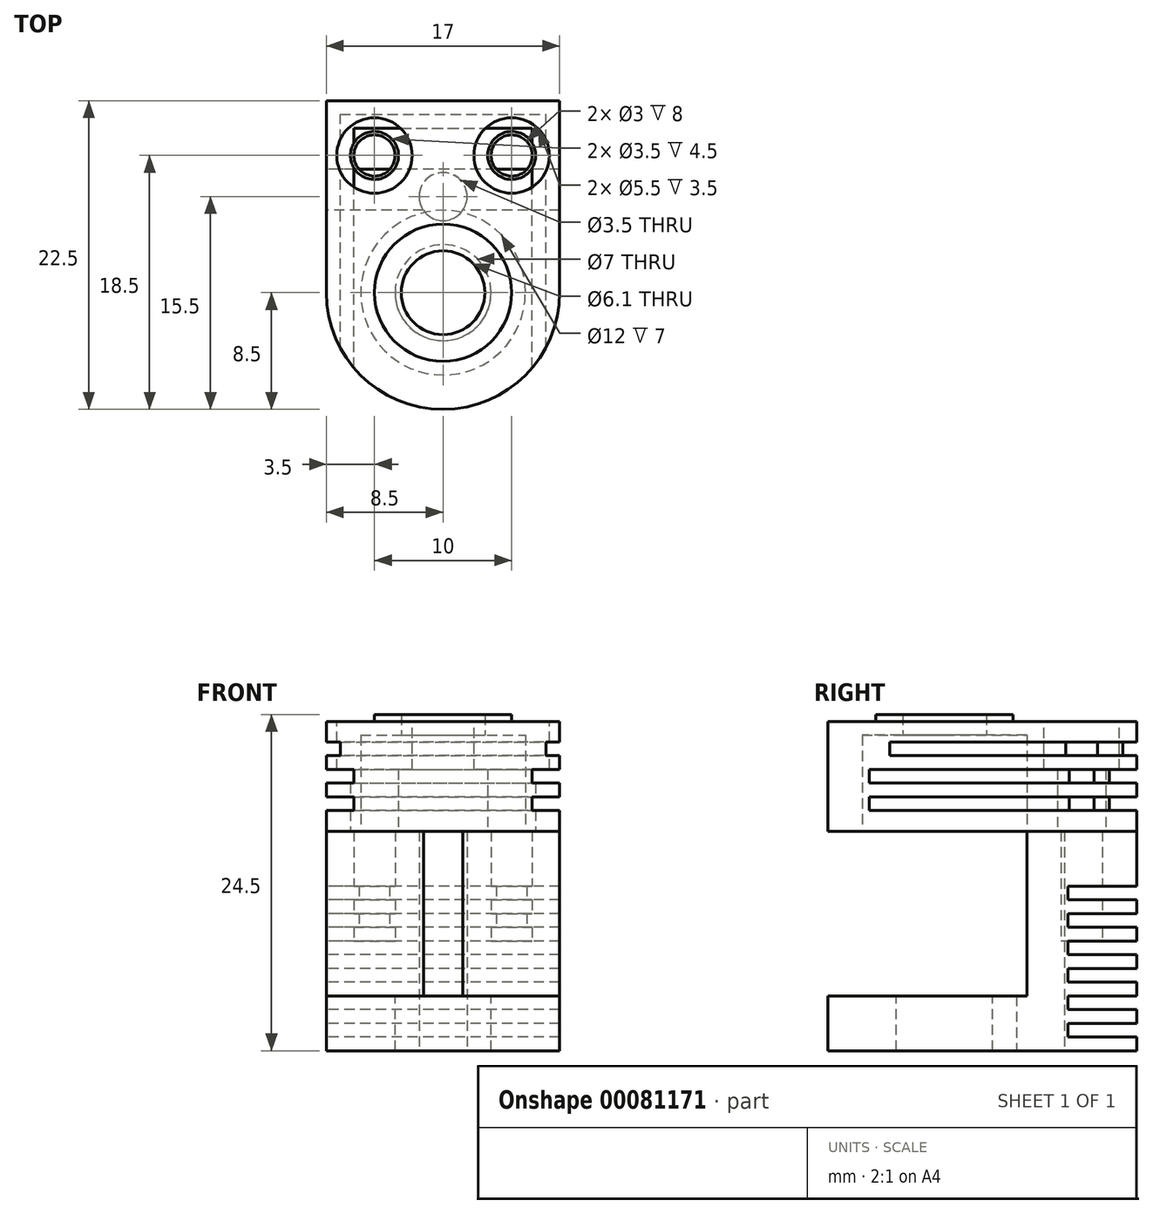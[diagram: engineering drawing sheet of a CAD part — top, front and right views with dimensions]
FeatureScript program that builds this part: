
annotation { "Feature Type Name" : "Feature", "Feature Type Description" : "" }
export const myFeature = defineFeature(function(context is Context, id is Id, definition is map)
    precondition{}
    {
        {
            var Q0;
            Q0=qCreatedBy(makeId("Top.planeOp"),FACE);
            var sketch = newSketch(context, id + "F0", { "sketchPlane" : qUnion([Q0])});
            skArc(sketch, "E0", {"start": v(-8.5, 0) * mm, "mid": v(0, -8.5) * mm, "end": v(8.5, 0) * mm});
            skLineSegment(sketch, "E1", {"start": v(-8.5, 0) * mm, "end": v(-8.5, 14) * mm});
            skLineSegment(sketch, "E2", {"start": v(-8.5, 14) * mm, "end": v(8.5, 14) * mm});
            skLineSegment(sketch, "E3", {"start": v(8.5, 14) * mm, "end": v(8.5, 0) * mm});
            skSolve(sketch);
        }
        {
            var Q0;
            Q0=qSketchRegion(id+"F0",true);
            extrude(context, id + "F1", {"entities" : qUnion([Q0]), "depth" : 16 * mm});
        }
        {
            var Q0;
            Q0=makeQuery(id+"F1.opExtrude","CAP_FACE",FACE,{"disambiguationData":[OSD([sQuery(id+"F0.wireOp",EDGE,"E0")])],"isStart":true});
            var sketch = newSketch(context, id + "F2", { "sketchPlane" : qUnion([Q0])});
            skCircle(sketch, "E4", {"center": v(0, -7) * mm, "radius": 1.75 * mm});
            skCircle(sketch, "E5", {"center": v(5, -10) * mm, "radius": 1.5 * mm});
            skCircle(sketch, "E6", {"center": v(-5, -10) * mm, "radius": 1.5 * mm});
            skSolve(sketch);
        }
        {
            var Q0;
            Q0=qSketchRegion(id+"F2",true);
            extrude(context, id + "F3", {"entities" : qUnion([Q0]), "operationType" : NewBodyOperationType.REMOVE, "endBound" : BoundingType.THROUGH_ALL, "oppositeDirection" : true, "depth" : 25 * mm});
        }
        {
            var Q0;
            Q0=makeQuery(id+"F1.opExtrude","CAP_FACE",FACE,{"disambiguationData":[OSD([sQuery(id+"F0.wireOp",EDGE,"E0"),sQuery(id+"F0.wireOp",EDGE,"E1"),sQuery(id+"F0.wireOp",EDGE,"E2"),sQuery(id+"F0.wireOp",EDGE,"E3")])],"isStart":true});
            cPlane(context, id + "F4", {"entities" : qUnion([Q0]), "cplaneType" : CPlaneType.OFFSET, "offset" : 4 * mm, "oppositeDirection" : true, "width" : 150 * mm, "height" : 150 * mm});
        }
        {
            var Q0;
            Q0=qCreatedBy(id+"F4.planeOp",FACE);
            var sketch = newSketch(context, id + "F5", { "sketchPlane" : qUnion([Q0])});
            skCircle(sketch, "E7", {"center": v(0, 0) * mm, "radius": 3.5 * mm});
            skSolve(sketch);
        }
        {
            var Q0;
            Q0=qSketchRegion(id+"F5",true);
            extrude(context, id + "F6", {"entities" : qUnion([Q0]), "operationType" : NewBodyOperationType.REMOVE, "endBound" : BoundingType.THROUGH_ALL, "depth" : 25 * mm});
        }
        {
            var Q0;
            Q0=qCreatedBy(id+"F4.planeOp",FACE);
            var sketch = newSketch(context, id + "F7", { "sketchPlane" : qUnion([Q0])});
            skArc(sketch, "E8", {"start": v(8.5, 0) * mm, "mid": v(0, 8.5) * mm, "end": v(-8.5, 0) * mm});
            skLineSegment(sketch, "E9", {"start": v(-8.5, 0) * mm, "end": v(-8.5, -6) * mm});
            skLineSegment(sketch, "E10", {"start": v(-8.5, -6) * mm, "end": v(8.5, -6) * mm});
            skLineSegment(sketch, "E11", {"start": v(8.5, -6) * mm, "end": v(8.5, 0) * mm});
            skSolve(sketch);
        }
        {
            var Q0;
            Q0=qSketchRegion(id+"F7",true);
            extrude(context, id + "F8", {"entities" : qUnion([Q0]), "operationType" : NewBodyOperationType.REMOVE, "oppositeDirection" : true, "depth" : 13 * mm});
        }
        {
            var Q0;
            Q0=makeQuery(id+"F1.opExtrude","CAP_FACE",FACE,{"disambiguationData":[OSD([sQuery(id+"F0.wireOp",EDGE,"E0"),sQuery(id+"F0.wireOp",EDGE,"E1"),sQuery(id+"F0.wireOp",EDGE,"E2"),sQuery(id+"F0.wireOp",EDGE,"E3")])],"isStart":false});
            var sketch = newSketch(context, id + "F9", { "sketchPlane" : qUnion([Q0])});
            skArc(sketch, "E12", {"start": v(-8.5, 0) * mm, "mid": v(0, -8.5) * mm, "end": v(8.5, 0) * mm});
            skLineSegment(sketch, "E13", {"start": v(-8.5, 14) * mm, "end": v(-8.5, 0) * mm});
            skLineSegment(sketch, "E14", {"start": v(-8.5, 14) * mm, "end": v(8.5, 14) * mm});
            skLineSegment(sketch, "E15", {"start": v(8.5, 14) * mm, "end": v(8.5, 0) * mm});
            skCircle(sketch, "E16", {"center": v(0, 0) * mm, "radius": 3.05 * mm});
            skCircle(sketch, "E17", {"center": v(-5, 10) * mm, "radius": 1.75 * mm});
            skCircle(sketch, "E18", {"center": v(5, 10) * mm, "radius": 1.75 * mm});
            skSolve(sketch);
        }
        {
            var Q0;
            Q0=qSketchRegion(id+"F9",true);
            extrude(context, id + "F10", {"entities" : qUnion([Q0]), "depth" : 8 * mm});
        }
        {
            var Q0;
            Q0=makeQuery(id+"F10.opExtrude","CAP_FACE",FACE,{"disambiguationData":[OSD([sQuery(id+"F9.wireOp",EDGE,"E12"),sQuery(id+"F9.wireOp",EDGE,"E13"),sQuery(id+"F9.wireOp",EDGE,"E14"),sQuery(id+"F9.wireOp",EDGE,"E15"),sQuery(id+"F9.wireOp",EDGE,"E16"),sQuery(id+"F9.wireOp",EDGE,"E17"),sQuery(id+"F9.wireOp",EDGE,"E18")])],"isStart":false});
            var sketch = newSketch(context, id + "F11", { "sketchPlane" : qUnion([Q0])});
            skCircle(sketch, "E19", {"center": v(-5, 10) * mm, "radius": 2.75 * mm});
            skCircle(sketch, "E20", {"center": v(5, 10) * mm, "radius": 2.75 * mm});
            skSolve(sketch);
        }
        {
            var Q0;
            Q0=qSketchRegion(id+"F11",true);
            extrude(context, id + "F12", {"entities" : qUnion([Q0]), "operationType" : NewBodyOperationType.REMOVE, "oppositeDirection" : true, "depth" : 3.5 * mm});
        }
        {
            var Q0;
            Q0=makeQuery(id+"F10.opExtrude","CAP_FACE",FACE,{"disambiguationData":[OSD([sQuery(id+"F9.wireOp",EDGE,"E12"),sQuery(id+"F9.wireOp",EDGE,"E13"),sQuery(id+"F9.wireOp",EDGE,"E14"),sQuery(id+"F9.wireOp",EDGE,"E15"),sQuery(id+"F9.wireOp",EDGE,"E16"),sQuery(id+"F9.wireOp",EDGE,"E17"),sQuery(id+"F9.wireOp",EDGE,"E18")])],"isStart":true});
            var sketch = newSketch(context, id + "F13", { "sketchPlane" : qUnion([Q0])});
            skCircle(sketch, "E21", {"center": v(0, 0) * mm, "radius": 6 * mm});
            skSolve(sketch);
        }
        {
            var Q0;
            Q0=qSketchRegion(id+"F13",true);
            extrude(context, id + "F14", {"entities" : qUnion([Q0]), "operationType" : NewBodyOperationType.REMOVE, "oppositeDirection" : true, "depth" : 7 * mm});
        }
        {
            var Q0;
            Q0=makeQuery(id+"F1.opExtrude","CAP_FACE",FACE,{"disambiguationData":[OSD([sQuery(id+"F0.wireOp",EDGE,"E0"),sQuery(id+"F0.wireOp",EDGE,"E1"),sQuery(id+"F0.wireOp",EDGE,"E2"),sQuery(id+"F0.wireOp",EDGE,"E3")])],"isStart":true});
            var sketch = newSketch(context, id + "F15", { "sketchPlane" : qUnion([Q0])});
            skCircle(sketch, "E22", {"center": v(5, -10) * mm, "radius": 1.5 * mm});
            skCircle(sketch, "E23", {"center": v(-5, -10) * mm, "radius": 1.5 * mm});
            skSolve(sketch);
        }
        {
            var Q0;
            Q0=qSketchRegion(id+"F15",true);
            extrude(context, id + "F16", {"entities" : qUnion([Q0]), "operationType" : NewBodyOperationType.ADD, "oppositeDirection" : true, "depth" : 8 * mm});
        }
        {
            var Q0;
            Q0=makeQuery(id+"F1.opExtrude","SWEPT_FACE",FACE,{"disambiguationData":[OSD([sQuery(id+"F0.wireOp",EDGE,"E1")])]});
            var sketch = newSketch(context, id + "F17", { "sketchPlane" : qUnion([Q0])});
            skLineSegment(sketch, "E24.bottom", {"start": v(-14, 1) * mm, "end": v(-9, 1) * mm});
            skLineSegment(sketch, "E24.top", {"start": v(-14, 2) * mm, "end": v(-9, 2) * mm});
            skLineSegment(sketch, "E24.left", {"start": v(-14, 1) * mm, "end": v(-14, 2) * mm});
            skLineSegment(sketch, "E24.right", {"start": v(-9, 1) * mm, "end": v(-9, 2) * mm});
            skLineSegment(sketch, "E25.bottom", {"start": v(-14, 3) * mm, "end": v(-9, 3) * mm});
            skLineSegment(sketch, "E25.top", {"start": v(-14, 4) * mm, "end": v(-9, 4) * mm});
            skLineSegment(sketch, "E25.left", {"start": v(-14, 3) * mm, "end": v(-14, 4) * mm});
            skLineSegment(sketch, "E25.right", {"start": v(-9, 3) * mm, "end": v(-9, 4) * mm});
            skLineSegment(sketch, "E26.bottom", {"start": v(-14, 5) * mm, "end": v(-9, 5) * mm});
            skLineSegment(sketch, "E26.top", {"start": v(-14, 6) * mm, "end": v(-9, 6) * mm});
            skLineSegment(sketch, "E26.left", {"start": v(-14, 5) * mm, "end": v(-14, 6) * mm});
            skLineSegment(sketch, "E26.right", {"start": v(-9, 5) * mm, "end": v(-9, 6) * mm});
            skLineSegment(sketch, "E27.bottom", {"start": v(-14, 7) * mm, "end": v(-9, 7) * mm});
            skLineSegment(sketch, "E27.top", {"start": v(-14, 8) * mm, "end": v(-9, 8) * mm});
            skLineSegment(sketch, "E27.left", {"start": v(-14, 7) * mm, "end": v(-14, 8) * mm});
            skLineSegment(sketch, "E27.right", {"start": v(-9, 7) * mm, "end": v(-9, 8) * mm});
            skLineSegment(sketch, "E28.bottom", {"start": v(-14, 9) * mm, "end": v(-9, 9) * mm});
            skLineSegment(sketch, "E28.top", {"start": v(-14, 10) * mm, "end": v(-9, 10) * mm});
            skLineSegment(sketch, "E28.left", {"start": v(-14, 9) * mm, "end": v(-14, 10) * mm});
            skLineSegment(sketch, "E28.right", {"start": v(-9, 9) * mm, "end": v(-9, 10) * mm});
            skLineSegment(sketch, "E29.bottom", {"start": v(-14, 11) * mm, "end": v(-9, 11) * mm});
            skLineSegment(sketch, "E29.top", {"start": v(-14, 12) * mm, "end": v(-9, 12) * mm});
            skLineSegment(sketch, "E29.left", {"start": v(-14, 11) * mm, "end": v(-14, 12) * mm});
            skLineSegment(sketch, "E29.right", {"start": v(-9, 11) * mm, "end": v(-9, 12) * mm});
            skSolve(sketch);
        }
        {
            var Q0;
            Q0=qSketchRegion(id+"F17",true);
            extrude(context, id + "F18", {"entities" : qUnion([Q0]), "operationType" : NewBodyOperationType.REMOVE, "endBound" : BoundingType.THROUGH_ALL, "oppositeDirection" : true, "depth" : 25 * mm});
        }
        {
            var Q0;
            Q0=makeQuery(id+"F10.opExtrude","SWEPT_FACE",FACE,{"disambiguationData":[OSD([sQuery(id+"F9.wireOp",EDGE,"E14")])]});
            var sketch = newSketch(context, id + "F19", { "sketchPlane" : qUnion([Q0])});
            skLineSegment(sketch, "E30.bottom", {"start": v(-8.5, 20.5) * mm, "end": v(-6.5, 20.5) * mm});
            skLineSegment(sketch, "E30.top", {"start": v(-8.5, 19.5) * mm, "end": v(-6.5, 19.5) * mm});
            skLineSegment(sketch, "E30.left", {"start": v(-8.5, 20.5) * mm, "end": v(-8.5, 19.5) * mm});
            skLineSegment(sketch, "E30.right", {"start": v(-6.5, 20.5) * mm, "end": v(-6.5, 19.5) * mm});
            skLineSegment(sketch, "E31.bottom", {"start": v(-8.5, 18.5) * mm, "end": v(-6.5, 18.5) * mm});
            skLineSegment(sketch, "E31.top", {"start": v(-8.5, 17.5) * mm, "end": v(-6.5, 17.5) * mm});
            skLineSegment(sketch, "E31.left", {"start": v(-8.5, 18.5) * mm, "end": v(-8.5, 17.5) * mm});
            skLineSegment(sketch, "E31.right", {"start": v(-6.5, 18.5) * mm, "end": v(-6.5, 17.5) * mm});
            skLineSegment(sketch, "E32.bottom", {"start": v(-8.5, 21.5) * mm, "end": v(-7.5, 21.5) * mm});
            skLineSegment(sketch, "E32.top", {"start": v(-8.5, 22.5) * mm, "end": v(-7.5, 22.5) * mm});
            skLineSegment(sketch, "E32.left", {"start": v(-8.5, 21.5) * mm, "end": v(-8.5, 22.5) * mm});
            skLineSegment(sketch, "E32.right", {"start": v(-7.5, 21.5) * mm, "end": v(-7.5, 22.5) * mm});
            skLineSegment(sketch, "E33.bottom", {"start": v(8.5, 17.5) * mm, "end": v(6.5, 17.5) * mm});
            skLineSegment(sketch, "E33.top", {"start": v(8.5, 18.5) * mm, "end": v(6.5, 18.5) * mm});
            skLineSegment(sketch, "E33.left", {"start": v(8.5, 17.5) * mm, "end": v(8.5, 18.5) * mm});
            skLineSegment(sketch, "E33.right", {"start": v(6.5, 17.5) * mm, "end": v(6.5, 18.5) * mm});
            skLineSegment(sketch, "E34.bottom", {"start": v(8.5, 19.5) * mm, "end": v(6.5, 19.5) * mm});
            skLineSegment(sketch, "E34.top", {"start": v(8.5, 20.5) * mm, "end": v(6.5, 20.5) * mm});
            skLineSegment(sketch, "E34.left", {"start": v(8.5, 19.5) * mm, "end": v(8.5, 20.5) * mm});
            skLineSegment(sketch, "E34.right", {"start": v(6.5, 19.5) * mm, "end": v(6.5, 20.5) * mm});
            skLineSegment(sketch, "E35.bottom", {"start": v(8.5, 21.5) * mm, "end": v(7.5, 21.5) * mm});
            skLineSegment(sketch, "E35.top", {"start": v(8.5, 22.5) * mm, "end": v(7.5, 22.5) * mm});
            skLineSegment(sketch, "E35.left", {"start": v(8.5, 21.5) * mm, "end": v(8.5, 22.5) * mm});
            skLineSegment(sketch, "E35.right", {"start": v(7.5, 21.5) * mm, "end": v(7.5, 22.5) * mm});
            skSolve(sketch);
        }
        {
            var Q0;
            Q0=qSketchRegion(id+"F19",true);
            extrude(context, id + "F20", {"entities" : qUnion([Q0]), "operationType" : NewBodyOperationType.REMOVE, "endBound" : BoundingType.THROUGH_ALL, "oppositeDirection" : true, "depth" : 25 * mm});
        }
        {
            var Q0;
            {var subQ0=sQuery(id+"F9.wireOp",EDGE,"E15");Q0=makeQuery(id+"F20.boolean.opBoolean","SPLIT",FACE,{"disambiguationData":[TD([makeQuery(id+"F20.opExtrude","SWEPT_FACE",FACE,{"disambiguationData":[OSD([sQuery(id+"F19.wireOp",EDGE,"E31.top")])]})])],"derivedFrom":makeQuery(id+"F10.opExtrude","SWEPT_FACE",FACE,{"disambiguationData":[OSD([subQ0])]})});}
            var sketch = newSketch(context, id + "F21", { "sketchPlane" : qUnion([Q0])});
            skLineSegment(sketch, "E36.bottom", {"start": v(14, 17.5) * mm, "end": v(12, 17.5) * mm});
            skLineSegment(sketch, "E36.top", {"start": v(14, 18.5) * mm, "end": v(12, 18.5) * mm});
            skLineSegment(sketch, "E36.left", {"start": v(14, 17.5) * mm, "end": v(14, 18.5) * mm});
            skLineSegment(sketch, "E36.right", {"start": v(12, 17.5) * mm, "end": v(12, 18.5) * mm});
            skLineSegment(sketch, "E37.bottom", {"start": v(14, 19.5) * mm, "end": v(12, 19.5) * mm});
            skLineSegment(sketch, "E37.top", {"start": v(14, 20.5) * mm, "end": v(12, 20.5) * mm});
            skLineSegment(sketch, "E37.left", {"start": v(14, 19.5) * mm, "end": v(14, 20.5) * mm});
            skLineSegment(sketch, "E37.right", {"start": v(12, 19.5) * mm, "end": v(12, 20.5) * mm});
            skLineSegment(sketch, "E38.bottom", {"start": v(14, 21.5) * mm, "end": v(13, 21.5) * mm});
            skLineSegment(sketch, "E38.top", {"start": v(14, 22.5) * mm, "end": v(13, 22.5) * mm});
            skLineSegment(sketch, "E38.left", {"start": v(14, 21.5) * mm, "end": v(14, 22.5) * mm});
            skLineSegment(sketch, "E38.right", {"start": v(13, 21.5) * mm, "end": v(13, 22.5) * mm});
            skSolve(sketch);
        }
        {
            var Q0;
            Q0=qSketchRegion(id+"F21",true);
            extrude(context, id + "F22", {"entities" : qUnion([Q0]), "operationType" : NewBodyOperationType.REMOVE, "endBound" : BoundingType.THROUGH_ALL, "oppositeDirection" : true, "depth" : 25 * mm});
        }
        {
            var Q0;
            Q0=makeQuery(id+"F10.opExtrude","CAP_FACE",FACE,{"disambiguationData":[OSD([sQuery(id+"F9.wireOp",EDGE,"E12"),sQuery(id+"F9.wireOp",EDGE,"E13"),sQuery(id+"F9.wireOp",EDGE,"E14"),sQuery(id+"F9.wireOp",EDGE,"E15"),sQuery(id+"F9.wireOp",EDGE,"E16"),sQuery(id+"F9.wireOp",EDGE,"E17"),sQuery(id+"F9.wireOp",EDGE,"E18")])],"isStart":false});
            var sketch = newSketch(context, id + "F23", { "sketchPlane" : qUnion([Q0])});
            skCircle(sketch, "E39", {"center": v(0, 0) * mm, "radius": 5 * mm});
            skSolve(sketch);
        }
        {
            var Q0;
            Q0=makeQuery(id+"F23.imprint","IMPRINT",FACE,{"disambiguationData":[TD([[makeQuery(id+"F23.imprint","IMPRINT",EDGE,{"derivedFrom":sQuery(id+"F23.wireOp",EDGE,"E39")}),1.0]])]});
            extrude(context, id + "F24", {"entities" : qUnion([Q0]), "operationType" : NewBodyOperationType.ADD, "depth" : .5 * mm});
        }
    });
